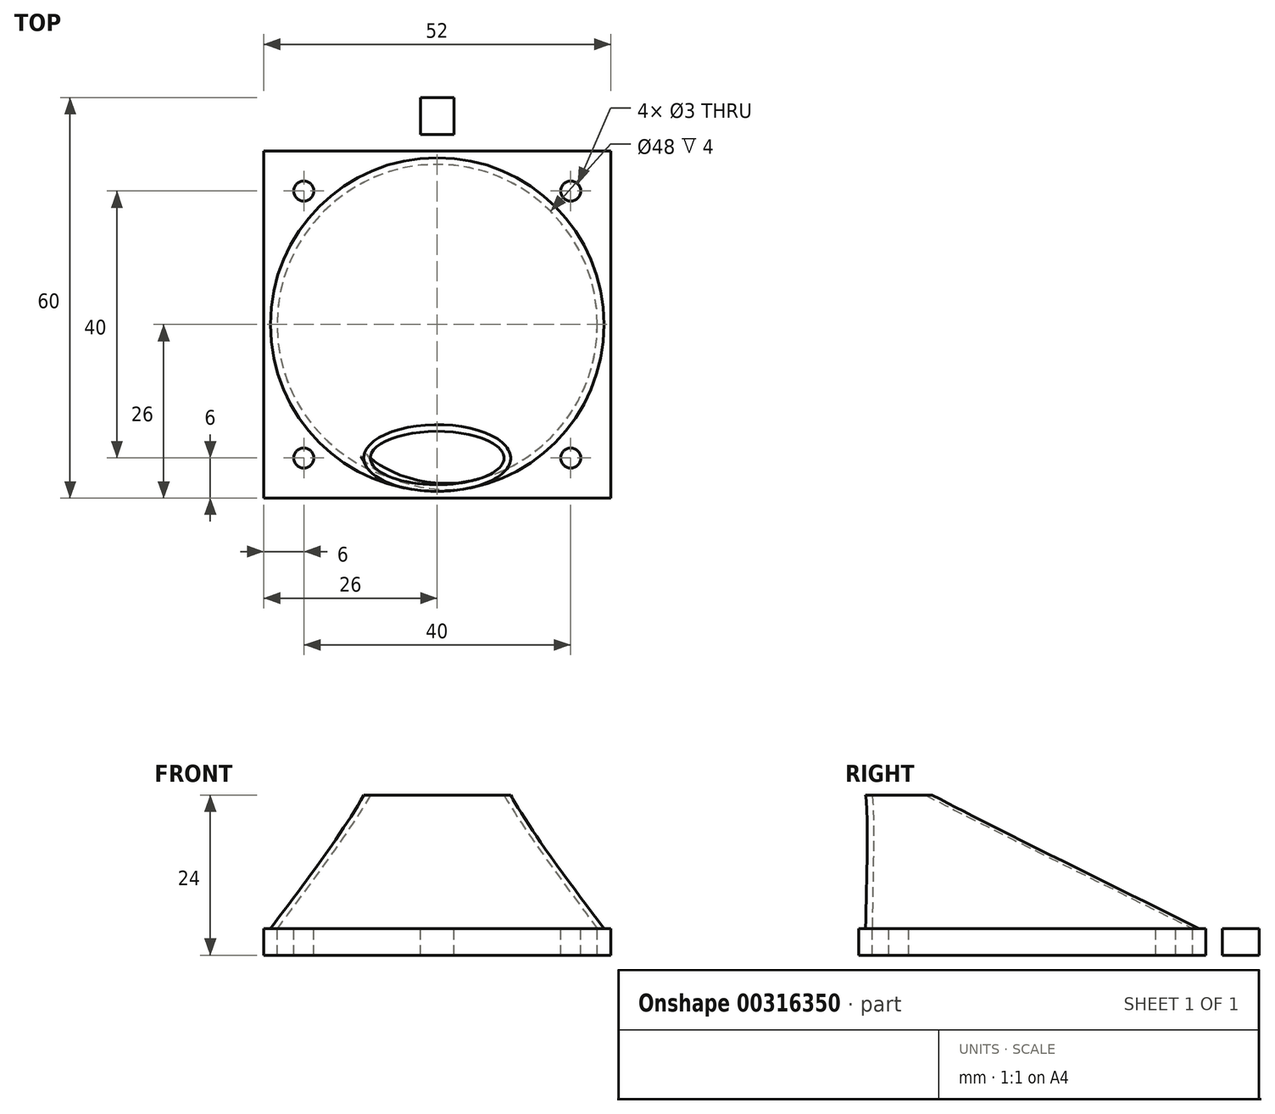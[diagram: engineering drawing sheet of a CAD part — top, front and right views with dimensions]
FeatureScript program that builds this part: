
annotation { "Feature Type Name" : "Feature", "Feature Type Description" : "" }
export const myFeature = defineFeature(function(context is Context, id is Id, definition is map)
    precondition{}
    {
        {
            var Q0;
            Q0=qCreatedBy(makeId("Top.planeOp"),FACE);
            var sketch = newSketch(context, id + "F0", { "sketchPlane" : qUnion([Q0])});
            skPoint(sketch, "E0.middle", {"position": v(0, 0) * mm});
            skCircle(sketch, "E1", {"center": v(0, 0) * mm, "radius": 24 * mm});
            skLineSegment(sketch, "E2.bottom", {"start": v(26, -26) * mm, "end": v(-26, -26) * mm});
            skLineSegment(sketch, "E2.top", {"start": v(26, 26) * mm, "end": v(-26, 26) * mm});
            skLineSegment(sketch, "E2.left", {"start": v(26, -26) * mm, "end": v(26, 26) * mm});
            skLineSegment(sketch, "E2.right", {"start": v(-26, -26) * mm, "end": v(-26, 26) * mm});
            skCircle(sketch, "E3", {"center": v(20, -20) * mm, "radius": 1.5 * mm});
            skCircle(sketch, "E4.MirrorC", {"center": v(-20, -20) * mm, "radius": 1.5 * mm});
            skCircle(sketch, "E5.MirrorC", {"center": v(20, 20) * mm, "radius": 1.5 * mm});
            skCircle(sketch, "E6.MirrorC", {"center": v(-20, 20) * mm, "radius": 1.5 * mm});
            skLineSegment(sketch, "E7.bottom", {"start": v(2.5, 26) * mm, "end": v(-2.5, 26) * mm});
            skLineSegment(sketch, "E7.top", {"start": v(2.5, 34) * mm, "end": v(-2.5, 34) * mm});
            skLineSegment(sketch, "E7.left", {"start": v(2.5, 26) * mm, "end": v(2.5, 34) * mm});
            skLineSegment(sketch, "E7.right", {"start": v(-2.5, 26) * mm, "end": v(-2.5, 34) * mm});
            skPoint(sketch, "E7.middle", {"position": v(0, 30) * mm});
            skLineSegment(sketch, "E8.0", {"start": v(2.5, 30) * mm, "end": v(-2.5, 30) * mm});
            skLineSegment(sketch, "E9.0", {"start": v(2.5, 31.5) * mm, "end": v(-2.5, 31.5) * mm});
            skLineSegment(sketch, "E10.0", {"start": v(2.5, 28.5) * mm, "end": v(-2.5, 28.5) * mm});
            skSolve(sketch);
        }
        {
            var Q0;
            Q0=qCreatedBy(makeId("Top.planeOp"),FACE);
            cPlane(context, id + "F1", {"entities" : qUnion([Q0]), "cplaneType" : CPlaneType.OFFSET, "offset" : 20 * mm, "width" : 150 * mm, "height" : 150 * mm});
        }
        {
            var Q0;
            Q0=qCreatedBy(id+"F1.planeOp",FACE);
            var sketch = newSketch(context, id + "F2", { "sketchPlane" : qUnion([Q0])});
            skEllipse(sketch, "E11", {"center": v(0, -20) * mm, "majorRadius": 10 * mm, "minorRadius": 4 * mm, "majorAxis": v(1, 0)});
            skSolve(sketch);
        }
        {
            var Q0;
            Q0=makeQuery(id+"F0.imprint","IMPRINT",FACE,{"disambiguationData":[TD([[makeQuery(id+"F0.imprint","IMPRINT",EDGE,{"derivedFrom":sQuery(id+"F0.wireOp",EDGE,"E1")}),1.0]])]});
            var Q1;
            Q1=makeQuery(id+"F2.imprint","IMPRINT",FACE,{"disambiguationData":[TD([[makeQuery(id+"F2.imprint","IMPRINT",EDGE,{"derivedFrom":sQuery(id+"F2.wireOp",EDGE,"E11")}),1.0]])]});
            loft(context, id + "F3", {"sheetProfilesArray" : [{ "sheetProfileEntities" : qUnion([Q0]) }, { "sheetProfileEntities" : qUnion([Q1]) }]});
        }
        {
            var Q0;
            Q0=qCreatedBy(makeId("Top.planeOp"),FACE);
            var sketch = newSketch(context, id + "F4", { "sketchPlane" : qUnion([Q0])});
            skCircle(sketch, "E12", {"center": v(0, 0) * mm, "radius": 25 * mm});
            skSolve(sketch);
        }
        {
            var Q0;
            Q0=qCreatedBy(id+"F1.planeOp",FACE);
            var sketch = newSketch(context, id + "F5", { "sketchPlane" : qUnion([Q0])});
            skEllipse(sketch, "E13", {"center": v(0, -20) * mm, "majorRadius": 11 * mm, "minorRadius": 5 * mm, "majorAxis": v(1, 0)});
            skSolve(sketch);
        }
        {
            var Q1;
            Q1=makeQuery(id+"F4.imprint","IMPRINT",FACE,{"disambiguationData":[TD([[makeQuery(id+"F4.imprint","IMPRINT",EDGE,{"derivedFrom":sQuery(id+"F4.wireOp",EDGE,"E12")}),1.0]])]});
            var Q2;
            Q2=makeQuery(id+"F5.imprint","IMPRINT",FACE,{"disambiguationData":[TD([[makeQuery(id+"F5.imprint","IMPRINT",EDGE,{"derivedFrom":sQuery(id+"F5.wireOp",EDGE,"E13")}),1.0]])]});
            loft(context, id + "F6", {"sheetProfilesArray" : [{ "sheetProfileEntities" : qUnion([Q1]) }, { "sheetProfileEntities" : qUnion([Q2]) }]});
        }
        {
            var Q0;
            Q0=makeQuery(id+"F3.opLoft","SWEPT_BODY",BODY,{"disambiguationData":[OSD([makeQuery(id+"F0.imprint","IMPRINT",FACE,{"disambiguationData":[TD([[makeQuery(id+"F0.imprint","IMPRINT",EDGE,{"derivedFrom":sQuery(id+"F0.wireOp",EDGE,"E1")}),1.0]])]}),makeQuery(id+"F2.imprint","IMPRINT",FACE,{"disambiguationData":[TD([[makeQuery(id+"F2.imprint","IMPRINT",EDGE,{"derivedFrom":sQuery(id+"F2.wireOp",EDGE,"E11")}),1.0]])]})])]});
            var Q1;
            Q1=makeQuery(id+"F6.opLoft","SWEPT_BODY",BODY,{"disambiguationData":[OSD([makeQuery(id+"F4.imprint","IMPRINT",FACE,{"disambiguationData":[TD([[makeQuery(id+"F4.imprint","IMPRINT",EDGE,{"derivedFrom":sQuery(id+"F4.wireOp",EDGE,"E12")}),1.0]])]}),makeQuery(id+"F5.imprint","IMPRINT",FACE,{"disambiguationData":[TD([[makeQuery(id+"F5.imprint","IMPRINT",EDGE,{"derivedFrom":sQuery(id+"F5.wireOp",EDGE,"E13")}),1.0]])]})])]});
            booleanBodies(context, id + "F7", {"operationType" : BooleanOperationType.SUBTRACTION, "tools" : qUnion([Q0]), "targets" : qUnion([Q1])});
        }
        {
            var Q0;
            Q0=makeQuery(id+"F0.imprint","IMPRINT",FACE,{"disambiguationData":[TD([[makeQuery(id+"F0.imprint","IMPRINT",EDGE,{"derivedFrom":sQuery(id+"F0.wireOp",EDGE,"E1")}),-1.0]])]});
            var Q1;
            {var subQ0=sQuery(id+"F0.wireOp",EDGE,"E7.bottom");Q1=makeQuery(id+"F0.imprint","IMPRINT",FACE,{"disambiguationData":[TD([[makeQuery(id+"F0.imprint","IMPRINT",EDGE,{"derivedFrom":subQ0}),-1.0]])]});}
            var Q2;
            {var subQ0=sQuery(id+"F0.wireOp",EDGE,"E8.0");Q2=makeQuery(id+"F0.imprint","IMPRINT",FACE,{"disambiguationData":[TD([[makeQuery(id+"F0.imprint","IMPRINT",EDGE,{"derivedFrom":subQ0}),1.0]])]});}
            var Q3;
            {var subQ0=sQuery(id+"F0.wireOp",EDGE,"E8.0");Q3=makeQuery(id+"F0.imprint","IMPRINT",FACE,{"disambiguationData":[TD([[makeQuery(id+"F0.imprint","IMPRINT",EDGE,{"derivedFrom":subQ0}),-1.0]])]});}
            var Q4;
            {var subQ0=sQuery(id+"F0.wireOp",EDGE,"E7.top");Q4=makeQuery(id+"F0.imprint","IMPRINT",FACE,{"disambiguationData":[TD([[makeQuery(id+"F0.imprint","IMPRINT",EDGE,{"derivedFrom":subQ0}),1.0]])]});}
            extrude(context, id + "F8", {"entities" : qUnion([Q0, Q1, Q2, Q3, Q4]), "operationType" : NewBodyOperationType.ADD, "oppositeDirection" : true, "depth" : 4 * mm});
        }
        {
            var Q0;
            {var subQ0=sQuery(id+"F0.wireOp",EDGE,"E8.0");Q0=makeQuery(id+"F0.imprint","IMPRINT",FACE,{"disambiguationData":[TD([[makeQuery(id+"F0.imprint","IMPRINT",EDGE,{"derivedFrom":subQ0}),1.0]])]});}
            var Q1;
            Q1=sQuery(id+"F0.wireOp",EDGE,"E8.0");
            revolve(context, id + "F9", {"entities" : qUnion([Q0]), "axis" : qUnion([Q1]), "revolveType" : RevolveType.FULL});
        }
        {
            var Q0;
            Q0=makeQuery(id+"F9.opRevolve","SWEPT_BODY",BODY,{"disambiguationData":[OSD([sQuery(id+"F0.wireOp",EDGE,"E7.left"),sQuery(id+"F0.wireOp",EDGE,"E7.right"),sQuery(id+"F0.wireOp",EDGE,"E8.0"),sQuery(id+"F0.wireOp",EDGE,"E10.0")])]});
            transform(context, id + "F10", {"entities" : qUnion([Q0]), "transformType" : TransformType.TRANSLATION_3D, "dx" : 0 * mm, "dy" : 0 * mm, "dz" : -2 * mm, "makeCopy" : false});
        }
        {
            var Q0;
            Q0=makeQuery(id+"F9.opRevolve","SWEPT_BODY",BODY,{"disambiguationData":[OSD([sQuery(id+"F0.wireOp",EDGE,"E7.left"),sQuery(id+"F0.wireOp",EDGE,"E7.right"),sQuery(id+"F0.wireOp",EDGE,"E8.0"),sQuery(id+"F0.wireOp",EDGE,"E10.0")])]});
            var Q1;
            Q1=makeQuery(id+"F6.opLoft","SWEPT_BODY",BODY,{"disambiguationData":[OSD([makeQuery(id+"F4.imprint","IMPRINT",FACE,{"disambiguationData":[TD([[makeQuery(id+"F4.imprint","IMPRINT",EDGE,{"derivedFrom":sQuery(id+"F4.wireOp",EDGE,"E12")}),1.0]])]}),makeQuery(id+"F5.imprint","IMPRINT",FACE,{"disambiguationData":[TD([[makeQuery(id+"F5.imprint","IMPRINT",EDGE,{"derivedFrom":sQuery(id+"F5.wireOp",EDGE,"E13")}),1.0]])]})])]});
            booleanBodies(context, id + "F11", {"operationType" : BooleanOperationType.SUBTRACTION, "tools" : qUnion([Q0]), "targets" : qUnion([Q1])});
        }
    });
